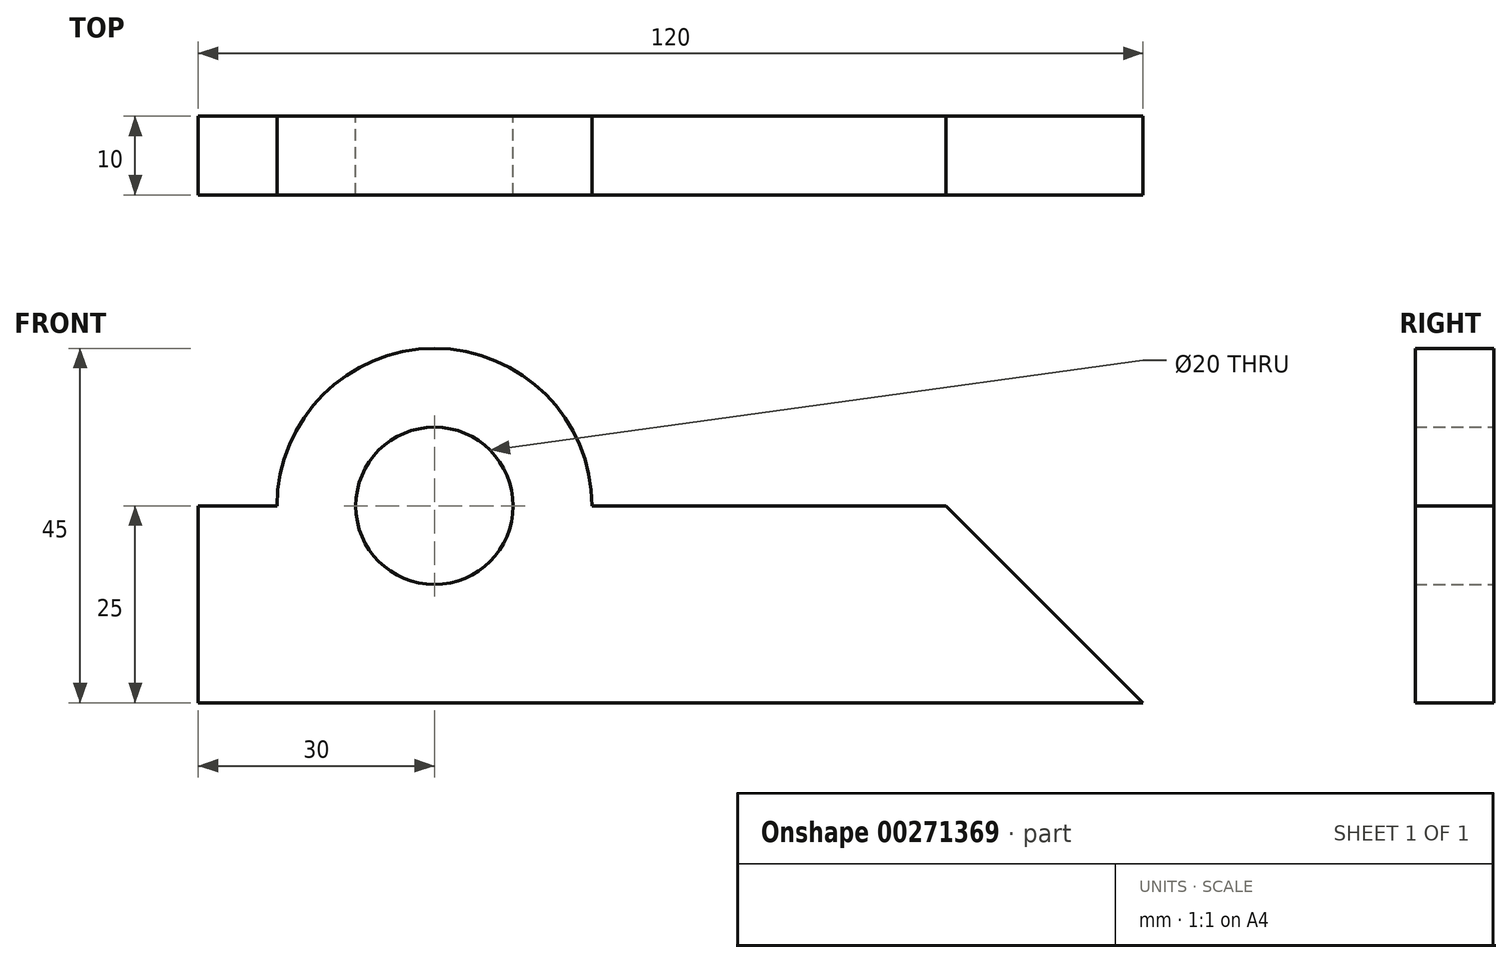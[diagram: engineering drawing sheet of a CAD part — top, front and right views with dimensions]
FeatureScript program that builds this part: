
annotation { "Feature Type Name" : "Feature", "Feature Type Description" : "" }
export const myFeature = defineFeature(function(context is Context, id is Id, definition is map)
    precondition{}
    {
        {
            var Q0;
            Q0=qCreatedBy(makeId("Front.planeOp"),FACE);
            var sketch = newSketch(context, id + "F0", { "sketchPlane" : qUnion([Q0])});
            skLineSegment(sketch, "E0", {"start": v(0, 0) * mm, "end": v(120, 0) * mm});
            skLineSegment(sketch, "E1", {"start": v(120, 0) * mm, "end": v(95, 25) * mm});
            skLineSegment(sketch, "E2", {"start": v(0, 0) * mm, "end": v(0, 25) * mm});
            skArc(sketch, "E3", {"start": v(10, 25) * mm, "mid": v(30, 45) * mm, "end": v(50, 25) * mm});
            skLineSegment(sketch, "E4", {"start": v(50, 25) * mm, "end": v(95, 25) * mm});
            skLineSegment(sketch, "E5", {"start": v(0, 25) * mm, "end": v(10, 25) * mm});
            skCircle(sketch, "E6", {"center": v(30, 25) * mm, "radius": 10 * mm});
            skSolve(sketch);
        }
        {
            var Q0;
            Q0=makeQuery(id+"F0.imprint","IMPRINT",FACE,{"disambiguationData":[TD([[makeQuery(id+"F0.imprint","IMPRINT",EDGE,{"derivedFrom":sQuery(id+"F0.wireOp",EDGE,"E0")}),1.0]])]});
            extrude(context, id + "F1", {"entities" : qUnion([Q0]), "depth" : 10 * mm});
        }
    });
